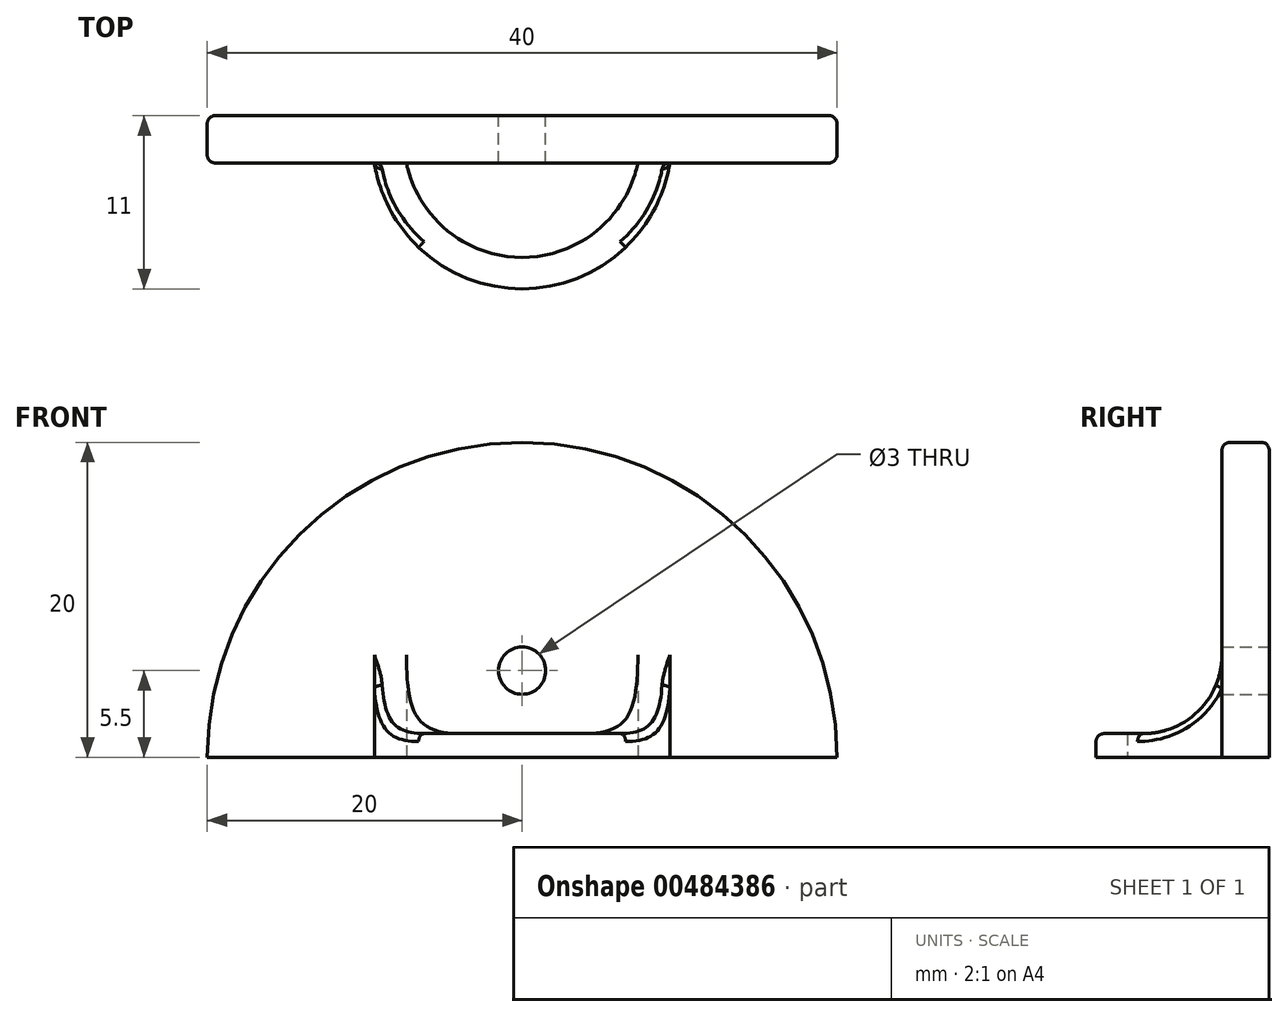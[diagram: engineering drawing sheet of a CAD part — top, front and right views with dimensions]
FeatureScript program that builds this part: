
annotation { "Feature Type Name" : "Feature", "Feature Type Description" : "" }
export const myFeature = defineFeature(function(context is Context, id is Id, definition is map)
    precondition{}
    {
        {
            var Q0;
            Q0=qCreatedBy(makeId("Front.planeOp"),FACE);
            var sketch = newSketch(context, id + "F0", { "sketchPlane" : qUnion([Q0])});
            skArc(sketch, "E0", {"start": v(20, 0) * mm, "mid": v(0, 20) * mm, "end": v(-20, 0) * mm});
            skLineSegment(sketch, "E1", {"start": v(-20, 0) * mm, "end": v(20, 0) * mm});
            skCircle(sketch, "E2", {"center": v(0, 5.5) * mm, "radius": 1.5 * mm});
            skSolve(sketch);
        }
        {
            var Q0;
            Q0=makeQuery(id+"F0.imprint","IMPRINT",FACE,{"disambiguationData":[TD([[makeQuery(id+"F0.imprint","IMPRINT",EDGE,{"derivedFrom":sQuery(id+"F0.wireOp",EDGE,"E0")}),1.0]])]});
            extrude(context, id + "F1", {"entities" : qUnion([Q0]), "depth" : 1.5 * mm, "offsetDistance" : 25 * mm, "hasSecondDirection" : true, "secondDirectionOppositeDirection" : true, "secondDirectionDepth" : 1.5 * mm});
        }
        {
            var Q0;
            Q0=makeQuery(id+"F1.opExtrude","CAP_EDGE",EDGE,{"disambiguationData":[OSD([sQuery(id+"F0.wireOp",EDGE,"E0")])],"isStart":false});
            var Q1;
            Q1=makeQuery(id+"F1.opExtrude","CAP_EDGE",EDGE,{"disambiguationData":[OSD([sQuery(id+"F0.wireOp",EDGE,"E0")])],"isStart":true});
            fillet(context, id + "F2", {"entities" : qUnion([Q0, Q1]), "radius" : .5 * mm, "tangentPropagation" : true, "allowEdgeOverflow" : false});
        }
        {
            var Q0;
            Q0=qCreatedBy(makeId("Top.planeOp"),FACE);
            var sketch = newSketch(context, id + "F3", { "sketchPlane" : qUnion([Q0])});
            skCircle(sketch, "E3", {"center": v(0, 0) * mm, "radius": 7.5 * mm});
            skCircle(sketch, "E4", {"center": v(0, 0) * mm, "radius": 9.5 * mm});
            skLineSegment(sketch, "E5", {"start": v(9.5, 0) * mm, "end": v(-9.5, 0) * mm});
            skSolve(sketch);
        }
        {
            var Q0;
            {var subQ0=sQuery(id+"F3.wireOp",EDGE,"E5");var subQ1=sQuery(id+"F3.wireOp",EDGE,"E3");var subQ2=makeQuery(id+"F3.imprint","INTERSECT",VERTEX,{"disambiguationData":[OD(0.0)],"derivedFrom":[subQ1,subQ0]});Q0=makeQuery(id+"F3.imprint","IMPRINT",FACE,{"disambiguationData":[TD([[makeQuery(id+"F3.imprint","IMPRINT",EDGE,{"disambiguationData":[TD([[subQ2,1.0]])],"derivedFrom":subQ1}),-1.0]])]});}
            extrude(context, id + "F4", {"entities" : qUnion([Q0]), "operationType" : NewBodyOperationType.ADD, "depth" : 1.5 * mm, "offsetDistance" : 25 * mm});
        }
        {
            var Q0;
            Q0=makeQuery(id+"F4.boolean.opBoolean","INTERSECT",EDGE,{"disambiguationData":[OD(1.0)],"derivedFrom":[makeQuery(id+"F1.opExtrude","CAP_FACE",FACE,{"disambiguationData":[OSD([sQuery(id+"F0.wireOp",EDGE,"E0"),sQuery(id+"F0.wireOp",EDGE,"E1"),sQuery(id+"F0.wireOp",EDGE,"E2")])],"isStart":false}),makeQuery(id+"F4.opExtrude","CAP_FACE",FACE,{"disambiguationData":[OSD([sQuery(id+"F3.wireOp",EDGE,"E3"),sQuery(id+"F3.wireOp",EDGE,"E4"),sQuery(id+"F3.wireOp",EDGE,"E5")])],"isStart":false})]});
            var Q1;
            Q1=makeQuery(id+"F4.boolean.opBoolean","INTERSECT",EDGE,{"disambiguationData":[OD(0.0)],"derivedFrom":[makeQuery(id+"F1.opExtrude","CAP_FACE",FACE,{"disambiguationData":[OSD([sQuery(id+"F0.wireOp",EDGE,"E0"),sQuery(id+"F0.wireOp",EDGE,"E1"),sQuery(id+"F0.wireOp",EDGE,"E2")])],"isStart":false}),makeQuery(id+"F4.opExtrude","CAP_FACE",FACE,{"disambiguationData":[OSD([sQuery(id+"F3.wireOp",EDGE,"E3"),sQuery(id+"F3.wireOp",EDGE,"E4"),sQuery(id+"F3.wireOp",EDGE,"E5")])],"isStart":false})]});
            fillet(context, id + "F5", {"entities" : qUnion([Q0, Q1]), "radius" : 5 * mm, "tangentPropagation" : true, "allowEdgeOverflow" : false});
        }
        {
            var Q0;
            Q0=makeQuery(id+"F4.opExtrude","CAP_EDGE",EDGE,{"disambiguationData":[OSD([sQuery(id+"F3.wireOp",EDGE,"E4")])],"isStart":false});
            fillet(context, id + "F6", {"entities" : qUnion([Q0]), "radius" : .5 * mm, "tangentPropagation" : true, "allowEdgeOverflow" : false});
        }
    });
